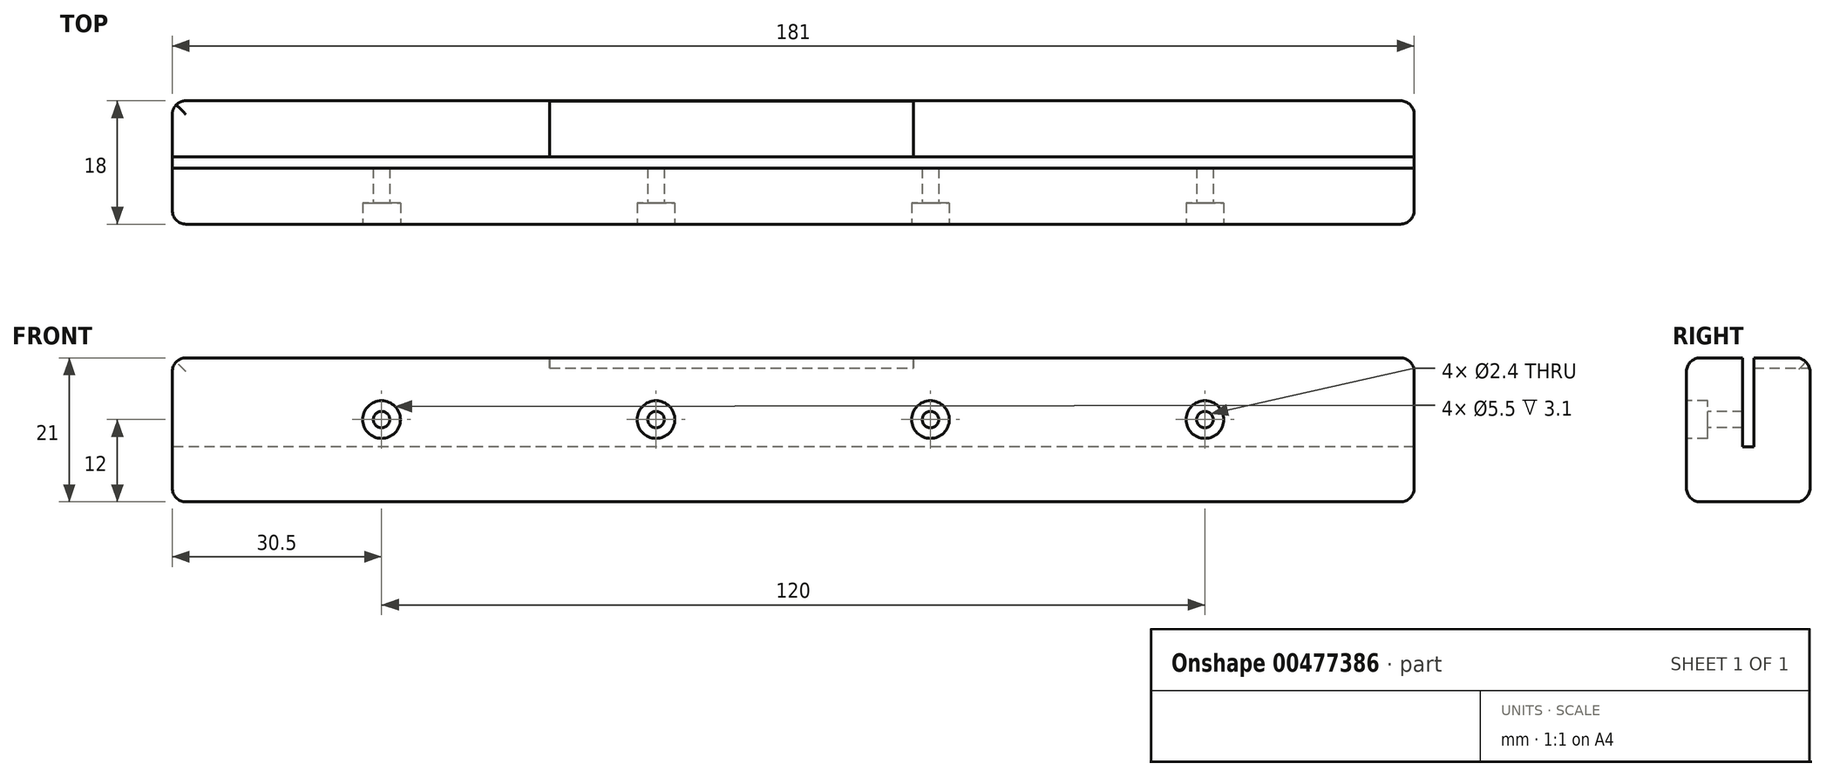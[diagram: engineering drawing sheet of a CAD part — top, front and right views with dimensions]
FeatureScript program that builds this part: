
annotation { "Feature Type Name" : "Feature", "Feature Type Description" : "" }
export const myFeature = defineFeature(function(context is Context, id is Id, definition is map)
    precondition{}
    {
        {
            var Q0;
            Q0=qCreatedBy(makeId("Right.planeOp"),FACE);
            var sketch = newSketch(context, id + "F0", { "sketchPlane" : qUnion([Q0])});
            skLineSegment(sketch, "E0", {"start": v(0, 0) * mm, "end": v(-9, 0) * mm});
            skLineSegment(sketch, "E1.bottom", {"start": v(-9, 0) * mm, "end": v(9, 0) * mm});
            skLineSegment(sketch, "E1.top", {"start": v(-9, 21) * mm, "end": v(-0.8, 21) * mm});
            skLineSegment(sketch, "E1.left", {"start": v(-9, 0) * mm, "end": v(-9, 21) * mm});
            skLineSegment(sketch, "E1.right", {"start": v(9, 0) * mm, "end": v(9, 21) * mm});
            skLineSegment(sketch, "E2", {"start": v(0, 8) * mm, "end": v(-0.8, 8) * mm});
            skLineSegment(sketch, "E3", {"start": v(-0.8, 8) * mm, "end": v(-0.8, 21) * mm});
            skLineSegment(sketch, "E4.MirrorCS", {"start": v(0.8, 8) * mm, "end": v(0.8, 21) * mm});
            skLineSegment(sketch, "E5.MirrorCS", {"start": v(0, 8) * mm, "end": v(0.8, 8) * mm});
            skLineSegment(sketch, "E6.trimOffspring", {"start": v(0.8, 21) * mm, "end": v(9, 21) * mm});
            skSolve(sketch);
        }
        {
            var Q0;
            Q0=makeQuery(id+"F0.imprint","IMPRINT",FACE,{"disambiguationData":[TD([[makeQuery(id+"F0.imprint","IMPRINT",EDGE,{"derivedFrom":sQuery(id+"F0.wireOp",EDGE,"E1.top")}),-1.0]])]});
            extrude(context, id + "F1", {"entities" : qUnion([Q0]), "endBound" : BoundingType.SYMMETRIC, "depth" : 181 * mm});
        }
        {
            var Q0;
            Q0=makeQuery(id+"F1.opExtrude","SWEPT_FACE",FACE,{"disambiguationData":[OSD([sQuery(id+"F0.wireOp",EDGE,"E1.right")])]});
            var sketch = newSketch(context, id + "F2", { "sketchPlane" : qUnion([Q0])});
            skLineSegment(sketch, "E7", {"start": v(35.5, 19.5) * mm, "end": v(-17.5, 19.5) * mm});
            skLineSegment(sketch, "E8", {"start": v(-17.5, 19.5) * mm, "end": v(-17.5, 21) * mm});
            skLineSegment(sketch, "E9", {"start": v(35.5, 19.5) * mm, "end": v(35.5, 21) * mm});
            skLineSegment(sketch, "E10", {"start": v(35.5, 21) * mm, "end": v(-17.5, 21) * mm});
            skSolve(sketch);
        }
        {
            var Q0;
            Q0=makeQuery(id+"F2.imprint","IMPRINT",FACE,{"disambiguationData":[TD([[makeQuery(id+"F2.imprint","IMPRINT",EDGE,{"derivedFrom":sQuery(id+"F2.wireOp",EDGE,"E7")}),-1.0]])]});
            extrude(context, id + "F3", {"entities" : qUnion([Q0]), "operationType" : NewBodyOperationType.REMOVE, "endBound" : BoundingType.UP_TO_NEXT, "oppositeDirection" : true, "depth" : 9 * mm});
        }
        {
            var Q0;
            Q0=makeQuery(id+"F1.opExtrude","SWEPT_FACE",FACE,{"disambiguationData":[OSD([sQuery(id+"F0.wireOp",EDGE,"E1.left")])]});
            var sketch = newSketch(context, id + "F4", { "sketchPlane" : qUnion([Q0])});
            skLineSegment(sketch, "E11", {"start": v(90.5, 21) * mm, "end": v(90.5, 12) * mm});
            skCircle(sketch, "E12", {"center": v(-60, 12) * mm, "radius": 1.2 * mm});
            skCircle(sketch, "E13", {"center": v(-20, 12) * mm, "radius": 1.2 * mm});
            skCircle(sketch, "E14", {"center": v(20, 12) * mm, "radius": 1.2 * mm});
            skCircle(sketch, "E15", {"center": v(60, 12) * mm, "radius": 1.2 * mm});
            skCircle(sketch, "E16", {"center": v(-60, 12) * mm, "radius": 2.75 * mm});
            skSolve(sketch);
        }
        {
            var Q0;
            Q0=makeQuery(id+"F4.imprint","IMPRINT",FACE,{"disambiguationData":[TD([[makeQuery(id+"F4.imprint","IMPRINT",EDGE,{"derivedFrom":sQuery(id+"F4.wireOp",EDGE,"E12")}),1.0]])]});
            var Q1;
            Q1=makeQuery(id+"F4.imprint","IMPRINT",FACE,{"disambiguationData":[TD([[makeQuery(id+"F4.imprint","IMPRINT",EDGE,{"derivedFrom":sQuery(id+"F4.wireOp",EDGE,"E13")}),1.0]])]});
            var Q2;
            Q2=makeQuery(id+"F4.imprint","IMPRINT",FACE,{"disambiguationData":[TD([[makeQuery(id+"F4.imprint","IMPRINT",EDGE,{"derivedFrom":sQuery(id+"F4.wireOp",EDGE,"E14")}),1.0]])]});
            var Q3;
            Q3=makeQuery(id+"F4.imprint","IMPRINT",FACE,{"disambiguationData":[TD([[makeQuery(id+"F4.imprint","IMPRINT",EDGE,{"derivedFrom":sQuery(id+"F4.wireOp",EDGE,"E15")}),1.0]])]});
            extrude(context, id + "F5", {"entities" : qUnion([Q0, Q1, Q2, Q3]), "operationType" : NewBodyOperationType.REMOVE, "endBound" : BoundingType.UP_TO_NEXT, "oppositeDirection" : true, "depth" : 25 * mm});
        }
        {
            var Q0;
            Q0=makeQuery(id+"F1.opExtrude","SWEPT_EDGE",EDGE,{"disambiguationData":[OSD([sQuery(id+"F0.wireOp",EDGE,"E1.top"),sQuery(id+"F0.wireOp",EDGE,"E1.left")])]});
            var Q1;
            Q1=makeQuery(id+"F1.opExtrude","CAP_EDGE",EDGE,{"disambiguationData":[OSD([sQuery(id+"F0.wireOp",EDGE,"E1.left")])],"isStart":true});
            var Q2;
            Q2=makeQuery(id+"F1.opExtrude","CAP_EDGE",EDGE,{"disambiguationData":[OSD([sQuery(id+"F0.wireOp",EDGE,"E1.bottom")])],"isStart":true});
            var Q3;
            Q3=makeQuery(id+"F1.opExtrude","CAP_EDGE",EDGE,{"disambiguationData":[OSD([sQuery(id+"F0.wireOp",EDGE,"E1.top")])],"isStart":true});
            var Q4;
            Q4=makeQuery(id+"F1.opExtrude","CAP_EDGE",EDGE,{"disambiguationData":[OSD([sQuery(id+"F0.wireOp",EDGE,"E6.trimOffspring")])],"isStart":true});
            var Q5;
            Q5=makeQuery(id+"F1.opExtrude","CAP_EDGE",EDGE,{"disambiguationData":[OSD([sQuery(id+"F0.wireOp",EDGE,"E1.right")])],"isStart":true});
            var Q6;
            Q6=makeQuery(id+"F1.opExtrude","SWEPT_EDGE",EDGE,{"disambiguationData":[OSD([sQuery(id+"F0.wireOp",EDGE,"E1.bottom"),sQuery(id+"F0.wireOp",EDGE,"E1.left")])]});
            var Q7;
            Q7=makeQuery(id+"F1.opExtrude","CAP_EDGE",EDGE,{"disambiguationData":[OSD([sQuery(id+"F0.wireOp",EDGE,"E1.left")])],"isStart":false});
            var Q8;
            Q8=makeQuery(id+"F1.opExtrude","CAP_EDGE",EDGE,{"disambiguationData":[OSD([sQuery(id+"F0.wireOp",EDGE,"E1.bottom")])],"isStart":false});
            var Q9;
            Q9=makeQuery(id+"F1.opExtrude","CAP_EDGE",EDGE,{"disambiguationData":[OSD([sQuery(id+"F0.wireOp",EDGE,"E1.right")])],"isStart":false});
            var Q10;
            Q10=makeQuery(id+"F1.opExtrude","CAP_EDGE",EDGE,{"disambiguationData":[OSD([sQuery(id+"F0.wireOp",EDGE,"E6.trimOffspring")])],"isStart":false});
            var Q11;
            Q11=makeQuery(id+"F1.opExtrude","CAP_EDGE",EDGE,{"disambiguationData":[OSD([sQuery(id+"F0.wireOp",EDGE,"E1.top")])],"isStart":false});
            var Q12;
            {var subQ0=sQuery(id+"F0.wireOp",EDGE,"E6.trimOffspring");var subQ1=sQuery(id+"F0.wireOp",EDGE,"E1.right");Q12=makeQuery(id+"F3.boolean.opBoolean","SPLIT",EDGE,{"disambiguationData":[TD([makeQuery(id+"F3.opExtrude","SWEPT_FACE",FACE,{"disambiguationData":[OSD([sQuery(id+"F2.wireOp",EDGE,"E8")])]})])],"derivedFrom":makeQuery(id+"F1.opExtrude","SWEPT_EDGE",EDGE,{"disambiguationData":[OSD([subQ1,subQ0])]})});}
            var Q13;
            Q13=makeQuery(id+"F1.opExtrude","SWEPT_EDGE",EDGE,{"disambiguationData":[OSD([sQuery(id+"F0.wireOp",EDGE,"E1.bottom"),sQuery(id+"F0.wireOp",EDGE,"E1.right")])]});
            fillet(context, id + "F6", {"entities" : qUnion([Q0, Q1, Q2, Q3, Q4, Q5, Q6, Q7, Q8, Q9, Q10, Q11, Q12, Q13]), "radius" : 2 * mm, "tangentPropagation" : true, "allowEdgeOverflow" : false});
        }
        {
            var Q0;
            Q0=makeQuery(id+"F1.opExtrude","SWEPT_FACE",FACE,{"disambiguationData":[OSD([sQuery(id+"F0.wireOp",EDGE,"E1.left")])]});
            var sketch = newSketch(context, id + "F7", { "sketchPlane" : qUnion([Q0])});
            skCircle(sketch, "E17", {"center": v(-60, 12) * mm, "radius": 2.75 * mm});
            skCircle(sketch, "E18", {"center": v(-20, 12) * mm, "radius": 2.75 * mm});
            skCircle(sketch, "E19", {"center": v(20, 12) * mm, "radius": 2.75 * mm});
            skCircle(sketch, "E20", {"center": v(60, 12) * mm, "radius": 2.75 * mm});
            skSolve(sketch);
        }
        {
            var Q0;
            Q0=makeQuery(id+"F7.imprint","IMPRINT",FACE,{"disambiguationData":[TD([[makeQuery(id+"F7.imprint","IMPRINT",EDGE,{"derivedFrom":sQuery(id+"F7.wireOp",EDGE,"E17")}),1.0]])]});
            var Q1;
            Q1=makeQuery(id+"F7.imprint","IMPRINT",FACE,{"disambiguationData":[TD([[makeQuery(id+"F7.imprint","IMPRINT",EDGE,{"derivedFrom":sQuery(id+"F7.wireOp",EDGE,"E18")}),1.0]])]});
            var Q2;
            Q2=makeQuery(id+"F7.imprint","IMPRINT",FACE,{"disambiguationData":[TD([[makeQuery(id+"F7.imprint","IMPRINT",EDGE,{"derivedFrom":sQuery(id+"F7.wireOp",EDGE,"E19")}),1.0]])]});
            var Q3;
            Q3=makeQuery(id+"F7.imprint","IMPRINT",FACE,{"disambiguationData":[TD([[makeQuery(id+"F7.imprint","IMPRINT",EDGE,{"derivedFrom":sQuery(id+"F7.wireOp",EDGE,"E20")}),1.0]])]});
            extrude(context, id + "F8", {"entities" : qUnion([Q0, Q1, Q2, Q3]), "operationType" : NewBodyOperationType.REMOVE, "oppositeDirection" : true, "depth" : 3.1 * mm});
        }
    });
